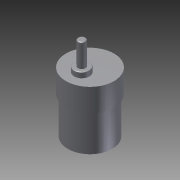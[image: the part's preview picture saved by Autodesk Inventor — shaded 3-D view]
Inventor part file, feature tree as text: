
AUTODESK INVENTOR PART (.ipt)
format: ipt  version: 2012 (Build 160160000, 160)  size: 232,960 bytes
history: native  units: mm
features: extrude x10, sketch x10, projected_geometry x7, fillet x5
ambient origin geometry x8: Origin, YZ Plane, XZ Plane, XY Plane, X Axis, Y Axis, Z Axis, Center Point
bodies: Solid1 (feature_tree)
feature tree (32):
  extrude  "Extrusion1"  Depth=28.77mm TaperAngle=0.0deg
  extrude  "Extrusion2"  Depth=18.0mm TaperAngle=0.0deg
  extrude  "Extrusion3"  Depth=31.3mm
  fillet  "Fillet1"  Radius=6.0mm
  extrude  "Extrusion4"  Depth=37.7mm
  extrude  "Extrusion5"  TaperAngle=0.0deg  [1 undecoded]
  extrude  "Extrusion6"  Depth=0.5mm
  extrude  "Extrusion7"  Depth=18.2mm TaperAngle=0.0deg
  fillet  "Fillet2"  Radius=5.45mm
  fillet  "Fillet3"  Radius=12.1mm
  extrude  "Extrusion8"  Depth=0.5mm TaperAngle=0.0deg
  extrude  "Extrusion9"  Depth=3.3mm TaperAngle=0.0deg
  fillet  "Fillet4"  Radius=3.0mm
  extrude  "Extrusion10"  Depth=2.0mm
  fillet  "Fillet5"  Radius=1.0mm
  sketch  "Sketch1"  dims[d0=34.9mm d1=28.77mm d2=0.0mm]
  sketch  "Sketch2"  dims[d3=37.7mm d4=18.0mm d5=0.0mm]
  sketch  "Sketch3"  dims[d6=12.0mm d7=31.3mm d8=6.0mm]
  projected_geometry  "Projected Loop1"
  sketch  "Sketch4"  dims[d9=6.0mm d10=37.7mm]
  sketch  "Sketch5"  dims[d11=37.7mm d12=0.0mm]
  sketch  "Sketch6"  dims[d13=4.1mm d14=0.0mm d15=0.5mm]
  projected_geometry  "Projected Loop2"
  sketch  "Sketch7"  dims[d16=6.0mm d17=18.2mm d18=0.0mm d19=5.45mm d20=12.1mm d21=0.0mm]
  sketch  "Sketch8"  dims[d24=33.5mm d25=0.5mm d26=0.0mm]
  projected_geometry  "Projected Loop3"
  sketch  "Sketch9"  dims[d27=7.9mm d28=3.3mm d29=0.0mm d30=3.0mm]
  projected_geometry  "Projected Loop4"
  projected_geometry  "Projected Loop5"
  sketch  "Sketch10"  dims[d31=3.0mm d32=2.0mm d33=1.0mm d34=0.0mm d35=0.5mm d36=2.85mm d37=12.0mm d40=6.4mm d41=6.4mm d42=9.5mm d43=34.9mm d44=34.9mm d45=34.9mm d46=7.35mm d47=13.2mm d48=6.9mm d49=0.0mm d50=1.0mm d51=1.0mm d52=6.9mm d53=0.0mm d54=0.75mm]
  projected_geometry  "Projected Loop6"
  projected_geometry  "Projected Loop7"
note: 1 required parameter value undecoded (feature->parameter linkage not recoverable at this tier; creation-order binding heuristic only, values carry confidence <= 0.55)
